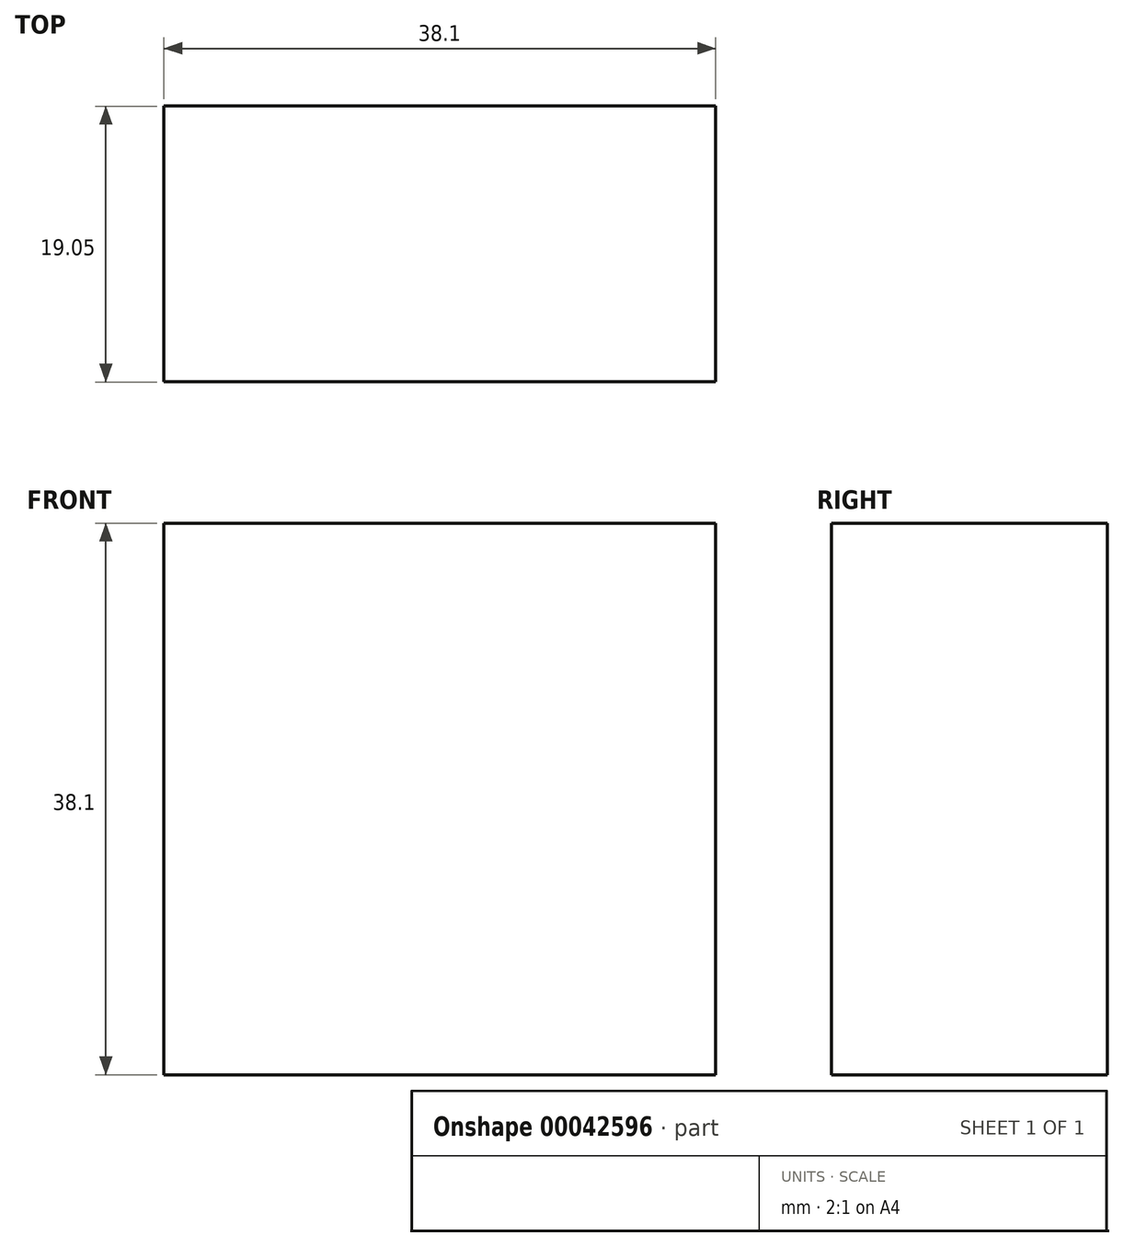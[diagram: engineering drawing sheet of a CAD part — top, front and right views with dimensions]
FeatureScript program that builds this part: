
annotation { "Feature Type Name" : "Feature", "Feature Type Description" : "" }
export const myFeature = defineFeature(function(context is Context, id is Id, definition is map)
    precondition{}
    {
        {
            var Q0;
            Q0=qCreatedBy(makeId("Top.planeOp"),FACE);
            var sketch = newSketch(context, id + "F0", { "sketchPlane" : qUnion([Q0])});
            skLineSegment(sketch, "E0.bottom", {"start": v(-43.98, -45.9) * mm, "end": v(-5.88, -45.9) * mm});
            skLineSegment(sketch, "E0.top", {"start": v(-43.98, -64.96) * mm, "end": v(-5.88, -64.96) * mm});
            skLineSegment(sketch, "E0.left", {"start": v(-43.98, -45.9) * mm, "end": v(-43.98, -64.96) * mm});
            skLineSegment(sketch, "E0.right", {"start": v(-5.88, -45.9) * mm, "end": v(-5.88, -64.96) * mm});
            skSolve(sketch);
        }
        {
            var Q0;
            Q0 = qSketchRegion(id + "F0", true);
            extrude(context, id + "F1", {"entities" : qUnion([Q0]), "depth" : 38.1 * mm});
        }
    });
